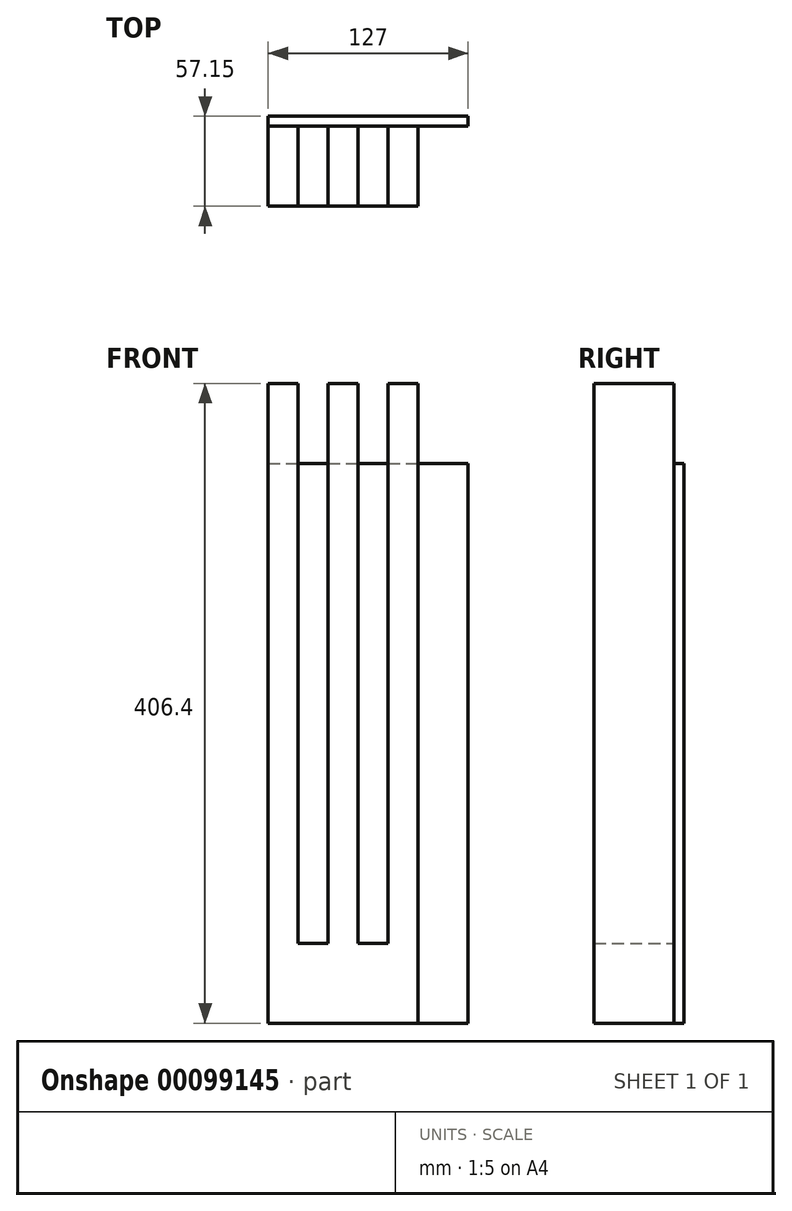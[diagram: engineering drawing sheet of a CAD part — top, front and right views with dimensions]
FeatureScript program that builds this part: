
annotation { "Feature Type Name" : "Feature", "Feature Type Description" : "" }
export const myFeature = defineFeature(function(context is Context, id is Id, definition is map)
    precondition{}
    {
        {
            var Q0;
            Q0=qCreatedBy(makeId("Top.planeOp"),FACE);
            var sketch = newSketch(context, id + "F0", { "sketchPlane" : qUnion([Q0])});
            skLineSegment(sketch, "E0.bottom", {"start": v(-47.62, 25.4) * mm, "end": v(-28.57, 25.4) * mm});
            skLineSegment(sketch, "E0.top", {"start": v(-47.62, -25.4) * mm, "end": v(-28.57, -25.4) * mm});
            skLineSegment(sketch, "E0.left", {"start": v(-47.62, 25.4) * mm, "end": v(-47.62, -25.4) * mm});
            skLineSegment(sketch, "E0.right", {"start": v(-28.57, 25.4) * mm, "end": v(-28.57, -25.4) * mm});
            skPoint(sketch, "E1", {"position": v(-28.57, 0) * mm});
            skPoint(sketch, "E2", {"position": v(-47.62, 0) * mm});
            skLineSegment(sketch, "E3.bottom", {"start": v(-28.57, 25.4) * mm, "end": v(-9.53, 25.4) * mm});
            skLineSegment(sketch, "E3.top", {"start": v(-28.57, -25.4) * mm, "end": v(-9.53, -25.4) * mm});
            skLineSegment(sketch, "E3.right", {"start": v(-9.53, 25.4) * mm, "end": v(-9.53, -25.4) * mm});
            skPoint(sketch, "E4", {"position": v(-9.52, 0) * mm});
            skLineSegment(sketch, "E5.bottom", {"start": v(-9.53, 25.4) * mm, "end": v(9.53, 25.4) * mm});
            skLineSegment(sketch, "E5.top", {"start": v(-9.53, -25.4) * mm, "end": v(9.53, -25.4) * mm});
            skLineSegment(sketch, "E5.left", {"start": v(-9.53, 25.4) * mm, "end": v(-9.52, -25.4) * mm});
            skLineSegment(sketch, "E5.right", {"start": v(9.52, 25.4) * mm, "end": v(9.53, -25.4) * mm});
            skPoint(sketch, "E6", {"position": v(9.52, 0) * mm});
            skLineSegment(sketch, "E7.bottom", {"start": v(9.53, 25.4) * mm, "end": v(28.58, 25.4) * mm});
            skLineSegment(sketch, "E7.top", {"start": v(9.53, -25.4) * mm, "end": v(28.58, -25.4) * mm});
            skLineSegment(sketch, "E7.right", {"start": v(28.57, 25.4) * mm, "end": v(28.58, -25.4) * mm});
            skPoint(sketch, "E8", {"position": v(28.58, 0) * mm});
            skLineSegment(sketch, "E9.bottom", {"start": v(28.58, 25.4) * mm, "end": v(47.63, 25.4) * mm});
            skLineSegment(sketch, "E9.top", {"start": v(28.58, -25.4) * mm, "end": v(47.63, -25.4) * mm});
            skLineSegment(sketch, "E9.left", {"start": v(28.58, 25.4) * mm, "end": v(28.57, -25.4) * mm});
            skLineSegment(sketch, "E9.right", {"start": v(47.63, 25.4) * mm, "end": v(47.63, -25.4) * mm});
            skPoint(sketch, "E10", {"position": v(47.63, 0) * mm});
            skLineSegment(sketch, "E11", {"start": v(-9.52, 0) * mm, "end": v(9.52, 0) * mm, "construction": true});
            skPoint(sketch, "E12", {"position": v(0, 0) * mm});
            skPoint(sketch, "E12.positionSnap0", {"position": v(0, 0) * mm});
            skSolve(sketch);
        }
        {
            var Q0;
            Q0=makeQuery(id+"F0.imprint","IMPRINT",FACE,{"disambiguationData":[TD([[makeQuery(id+"F0.imprint","IMPRINT",EDGE,{"derivedFrom":sQuery(id+"F0.wireOp",EDGE,"E0.bottom")}),-1.0]])]});
            var Q1;
            Q1=makeQuery(id+"F0.imprint","IMPRINT",FACE,{"disambiguationData":[TD([[makeQuery(id+"F0.imprint","IMPRINT",EDGE,{"derivedFrom":sQuery(id+"F0.wireOp",EDGE,"E5.bottom")}),-1.0]])]});
            var Q2;
            Q2=makeQuery(id+"F0.imprint","IMPRINT",FACE,{"disambiguationData":[TD([[makeQuery(id+"F0.imprint","IMPRINT",EDGE,{"derivedFrom":sQuery(id+"F0.wireOp",EDGE,"E9.bottom")}),-1.0]])]});
            var Q3;
            Q3=makeQuery(id+"F0.imprint","IMPRINT",FACE,{"disambiguationData":[TD([[makeQuery(id+"F0.imprint","IMPRINT",EDGE,{"derivedFrom":sQuery(id+"F0.wireOp",EDGE,"E3.bottom")}),-1.0]])]});
            var Q4;
            Q4=makeQuery(id+"F0.imprint","IMPRINT",FACE,{"disambiguationData":[TD([[makeQuery(id+"F0.imprint","IMPRINT",EDGE,{"derivedFrom":sQuery(id+"F0.wireOp",EDGE,"E7.bottom")}),-1.0]])]});
            extrude(context, id + "F1", {"entities" : qUnion([Q0, Q1, Q2, Q3, Q4]), "depth" : 50.8 * mm});
        }
        {
            var Q0;
            Q0=makeQuery(id+"F0.imprint","IMPRINT",FACE,{"disambiguationData":[TD([[makeQuery(id+"F0.imprint","IMPRINT",EDGE,{"derivedFrom":sQuery(id+"F0.wireOp",EDGE,"E5.bottom")}),-1.0]])]});
            var Q1;
            Q1=makeQuery(id+"F0.imprint","IMPRINT",FACE,{"disambiguationData":[TD([[makeQuery(id+"F0.imprint","IMPRINT",EDGE,{"derivedFrom":sQuery(id+"F0.wireOp",EDGE,"E0.bottom")}),-1.0]])]});
            var Q2;
            Q2=makeQuery(id+"F0.imprint","IMPRINT",FACE,{"disambiguationData":[TD([[makeQuery(id+"F0.imprint","IMPRINT",EDGE,{"derivedFrom":sQuery(id+"F0.wireOp",EDGE,"E9.bottom")}),-1.0]])]});
            extrude(context, id + "F2", {"entities" : qUnion([Q0, Q1, Q2]), "operationType" : NewBodyOperationType.ADD, "depth" : 406.4 * mm});
        }
        {
            var Q0;
            Q0=qCreatedBy(makeId("Top.planeOp"),FACE);
            var sketch = newSketch(context, id + "F3", { "sketchPlane" : qUnion([Q0])});
            skLineSegment(sketch, "E13.bottom", {"start": v(-47.62, 25.4) * mm, "end": v(79.38, 25.4) * mm});
            skLineSegment(sketch, "E13.top", {"start": v(-47.62, 31.75) * mm, "end": v(79.38, 31.75) * mm});
            skLineSegment(sketch, "E13.left", {"start": v(-47.62, 25.4) * mm, "end": v(-47.62, 31.75) * mm});
            skLineSegment(sketch, "E13.right", {"start": v(79.38, 25.4) * mm, "end": v(79.38, 31.75) * mm});
            skPoint(sketch, "E14.0", {"position": v(-47.62, 25.4) * mm});
            skLineSegment(sketch, "E15.0", {"start": v(-47.62, 25.4) * mm, "end": v(-28.57, 25.4) * mm});
            skSolve(sketch);
        }
        {
            var Q0;
            Q0=makeQuery(id+"F3.imprint","IMPRINT",FACE,{"disambiguationData":[TD([[makeQuery(id+"F3.imprint","IMPRINT",EDGE,{"derivedFrom":sQuery(id+"F3.wireOp",EDGE,"E13.bottom")}),1.0]])]});
            extrude(context, id + "F4", {"entities" : qUnion([Q0]), "depth" : 355.6 * mm});
        }
    });
